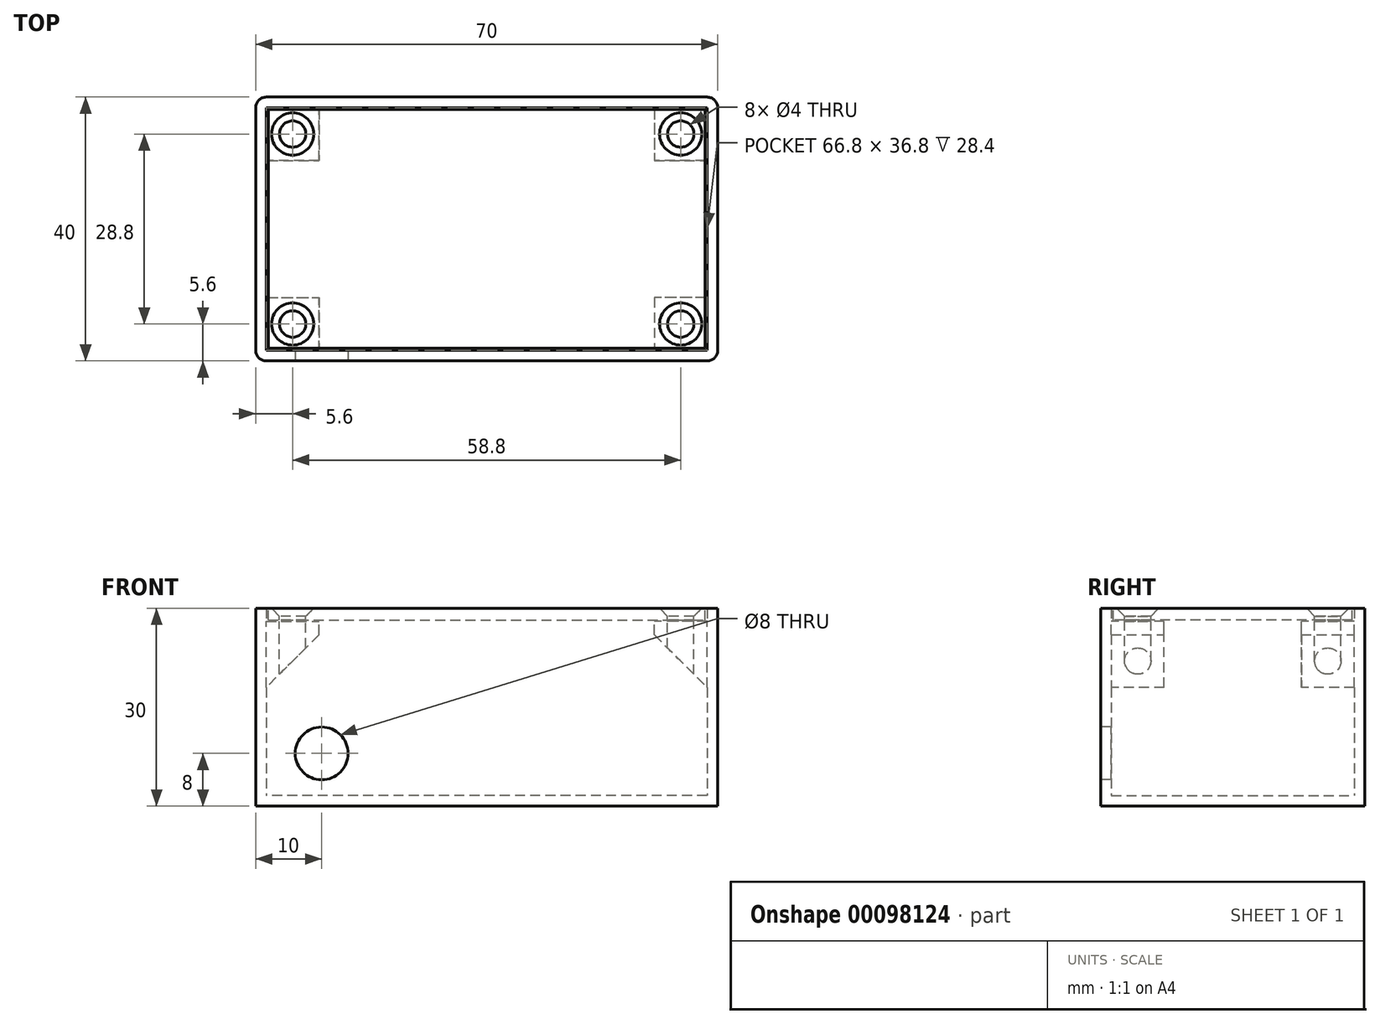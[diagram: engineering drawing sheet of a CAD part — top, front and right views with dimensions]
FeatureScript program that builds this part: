
annotation { "Feature Type Name" : "Feature", "Feature Type Description" : "" }
export const myFeature = defineFeature(function(context is Context, id is Id, definition is map)
    precondition{}
    {
        {
            var Q0;
            Q0=qCreatedBy(makeId("Top.planeOp"),FACE);
            var sketch = newSketch(context, id + "F0", { "sketchPlane" : qUnion([Q0])});
            skLineSegment(sketch, "E0.bottom", {"start": v(0, 0) * mm, "end": v(-70, 0) * mm});
            skLineSegment(sketch, "E0.top", {"start": v(0, 40) * mm, "end": v(-70, 40) * mm});
            skLineSegment(sketch, "E0.left", {"start": v(0, 0) * mm, "end": v(0, 40) * mm});
            skLineSegment(sketch, "E0.right", {"start": v(-70, 0) * mm, "end": v(-70, 40) * mm});
            skSolve(sketch);
        }
        {
            var Q0;
            Q0=makeQuery(id+"F0.imprint","IMPRINT",FACE,{"disambiguationData":[TD([[makeQuery(id+"F0.imprint","IMPRINT",EDGE,{"derivedFrom":sQuery(id+"F0.wireOp",EDGE,"E0.bottom")}),-1.0]])]});
            extrude(context, id + "F1", {"entities" : qUnion([Q0]), "depth" : 30 * mm});
        }
        {
            var Q0;
            Q0=makeQuery(id+"F1.opExtrude","CAP_FACE",FACE,{"disambiguationData":[OSD([sQuery(id+"F0.wireOp",EDGE,"E0.bottom"),sQuery(id+"F0.wireOp",EDGE,"E0.top"),sQuery(id+"F0.wireOp",EDGE,"E0.left"),sQuery(id+"F0.wireOp",EDGE,"E0.right")])],"isStart":false});
            shell(context, id + "F2", {"entities" : qUnion([Q0]), "thickness" : 1.6 * mm});
        }
        {
            var Q0;
            Q0=makeQuery(id+"F1.opExtrude","CAP_FACE",FACE,{"disambiguationData":[OSD([sQuery(id+"F0.wireOp",EDGE,"E0.bottom"),sQuery(id+"F0.wireOp",EDGE,"E0.top"),sQuery(id+"F0.wireOp",EDGE,"E0.left"),sQuery(id+"F0.wireOp",EDGE,"E0.right")])],"isStart":false});
            cPlane(context, id + "F3", {"entities" : qUnion([Q0]), "cplaneType" : CPlaneType.OFFSET, "offset" : 2 * mm, "oppositeDirection" : true, "width" : 150 * mm, "height" : 150 * mm});
        }
        {
            var Q0;
            Q0=qCreatedBy(id+"F3.planeOp",FACE);
            var sketch = newSketch(context, id + "F4", { "sketchPlane" : qUnion([Q0])});
            skLineSegment(sketch, "E1.bottom", {"start": v(-68.4, 38.4) * mm, "end": v(-60.4, 38.4) * mm});
            skLineSegment(sketch, "E1.top", {"start": v(-68.4, 30.4) * mm, "end": v(-60.4, 30.4) * mm});
            skLineSegment(sketch, "E1.left", {"start": v(-68.4, 38.4) * mm, "end": v(-68.4, 30.4) * mm});
            skLineSegment(sketch, "E1.right", {"start": v(-60.4, 38.4) * mm, "end": v(-60.4, 30.4) * mm});
            skLineSegment(sketch, "E2.bottom", {"start": v(-1.6, 38.4) * mm, "end": v(-9.6, 38.4) * mm});
            skLineSegment(sketch, "E2.top", {"start": v(-1.6, 30.4) * mm, "end": v(-9.6, 30.4) * mm});
            skLineSegment(sketch, "E2.left", {"start": v(-1.6, 38.4) * mm, "end": v(-1.6, 30.4) * mm});
            skLineSegment(sketch, "E2.right", {"start": v(-9.6, 38.4) * mm, "end": v(-9.6, 30.4) * mm});
            skLineSegment(sketch, "E3.bottom", {"start": v(-68.4, 9.6) * mm, "end": v(-60.4, 9.6) * mm});
            skLineSegment(sketch, "E3.top", {"start": v(-68.4, 1.6) * mm, "end": v(-60.4, 1.6) * mm});
            skLineSegment(sketch, "E3.left", {"start": v(-68.4, 9.6) * mm, "end": v(-68.4, 1.6) * mm});
            skLineSegment(sketch, "E3.right", {"start": v(-60.4, 9.6) * mm, "end": v(-60.4, 1.6) * mm});
            skLineSegment(sketch, "E4.bottom", {"start": v(-1.6, 9.6) * mm, "end": v(-9.6, 9.6) * mm});
            skLineSegment(sketch, "E4.top", {"start": v(-1.6, 1.6) * mm, "end": v(-9.6, 1.6) * mm});
            skLineSegment(sketch, "E4.left", {"start": v(-1.6, 9.6) * mm, "end": v(-1.6, 1.6) * mm});
            skLineSegment(sketch, "E4.right", {"start": v(-9.6, 9.6) * mm, "end": v(-9.6, 1.6) * mm});
            skCircle(sketch, "E5", {"center": v(-64.4, 34.4) * mm, "radius": 2 * mm});
            skPoint(sketch, "E5.centerSnap0", {"position": v(-64.4, 38.4) * mm});
            skPoint(sketch, "E5.centerSnap1", {"position": v(-60.4, 34.4) * mm});
            skCircle(sketch, "E6", {"center": v(-5.6, 34.4) * mm, "radius": 2 * mm});
            skPoint(sketch, "E6.centerSnap0", {"position": v(-5.6, 38.4) * mm});
            skPoint(sketch, "E6.centerSnap1", {"position": v(-1.6, 34.4) * mm});
            skCircle(sketch, "E7", {"center": v(-5.6, 5.6) * mm, "radius": 2 * mm});
            skPoint(sketch, "E7.centerSnap0", {"position": v(-5.6, 9.6) * mm});
            skPoint(sketch, "E7.centerSnap1", {"position": v(-1.6, 5.6) * mm});
            skCircle(sketch, "E8", {"center": v(-64.4, 5.6) * mm, "radius": 2 * mm});
            skPoint(sketch, "E8.centerSnap0", {"position": v(-60.4, 5.6) * mm});
            skPoint(sketch, "E8.centerSnap1", {"position": v(-64.4, 9.6) * mm});
            skSolve(sketch);
        }
        {
            var Q0;
            Q0 = qSketchRegion(id + "F4", true);
            extrude(context, id + "F5", {"entities" : qUnion([Q0]), "operationType" : NewBodyOperationType.ADD, "oppositeDirection" : true, "depth" : 10 * mm});
        }
        {
            var Q0;
            Q0=makeQuery(id+"F5.opExtrude","CAP_EDGE",EDGE,{"disambiguationData":[OSD([sQuery(id+"F4.wireOp",EDGE,"E1.right")])],"isStart":false});
            var Q1;
            Q1=makeQuery(id+"F5.opExtrude","CAP_EDGE",EDGE,{"disambiguationData":[OSD([sQuery(id+"F4.wireOp",EDGE,"E3.right")])],"isStart":false});
            var Q2;
            Q2=makeQuery(id+"F5.opExtrude","CAP_EDGE",EDGE,{"disambiguationData":[OSD([sQuery(id+"F4.wireOp",EDGE,"E2.right")])],"isStart":false});
            var Q3;
            Q3=makeQuery(id+"F5.opExtrude","CAP_EDGE",EDGE,{"disambiguationData":[OSD([sQuery(id+"F4.wireOp",EDGE,"E4.right")])],"isStart":false});
            chamfer(context, id + "F6", {"entities" : qUnion([Q0, Q1, Q2, Q3]), "width" : 8 * mm, "tangentPropagation" : true});
        }
        {
            var Q0;
            Q0=makeQuery(id+"F1.opExtrude","SWEPT_FACE",FACE,{"disambiguationData":[OSD([sQuery(id+"F0.wireOp",EDGE,"E0.bottom")])]});
            var sketch = newSketch(context, id + "F7", { "sketchPlane" : qUnion([Q0])});
            skCircle(sketch, "E9", {"center": v(-60, 8) * mm, "radius": 4 * mm});
            skSolve(sketch);
        }
        {
            var Q0;
            Q0 = qSketchRegion(id + "F7", true);
            extrude(context, id + "F8", {"entities" : qUnion([Q0]), "operationType" : NewBodyOperationType.REMOVE, "oppositeDirection" : true, "depth" : 25 * mm});
        }
        {
            var Q0;
            Q0=makeQuery(id+"F1.opExtrude","CAP_FACE",FACE,{"disambiguationData":[OSD([sQuery(id+"F0.wireOp",EDGE,"E0.bottom"),sQuery(id+"F0.wireOp",EDGE,"E0.top"),sQuery(id+"F0.wireOp",EDGE,"E0.left"),sQuery(id+"F0.wireOp",EDGE,"E0.right")])],"isStart":false});
            var sketch = newSketch(context, id + "F9", { "sketchPlane" : qUnion([Q0])});
            skLineSegment(sketch, "E10.bottom", {"start": v(-68.1, 38.1) * mm, "end": v(-1.9, 38.1) * mm});
            skLineSegment(sketch, "E10.top", {"start": v(-68.1, 1.9) * mm, "end": v(-1.9, 1.9) * mm});
            skLineSegment(sketch, "E10.left", {"start": v(-68.1, 38.1) * mm, "end": v(-68.1, 1.9) * mm});
            skLineSegment(sketch, "E10.right", {"start": v(-1.9, 38.1) * mm, "end": v(-1.9, 1.9) * mm});
            skCircle(sketch, "E11", {"center": v(-64.4, 34.4) * mm, "radius": 2 * mm});
            skCircle(sketch, "E12", {"center": v(-5.6, 34.4) * mm, "radius": 2 * mm});
            skCircle(sketch, "E13", {"center": v(-5.6, 5.6) * mm, "radius": 2 * mm});
            skCircle(sketch, "E14", {"center": v(-64.4, 5.6) * mm, "radius": 2 * mm});
            skSolve(sketch);
        }
        {
            var Q0;
            Q0 = qSketchRegion(id + "F9", true);
            extrude(context, id + "F10", {"entities" : qUnion([Q0]), "oppositeDirection" : true, "depth" : 1.8 * mm});
        }
        {
            var Q0;
            Q0=makeQuery(id+"F10.opExtrude","CAP_EDGE",EDGE,{"disambiguationData":[OSD([sQuery(id+"F9.wireOp",EDGE,"E13")])],"isStart":true});
            var Q1;
            Q1=makeQuery(id+"F10.opExtrude","CAP_EDGE",EDGE,{"disambiguationData":[OSD([sQuery(id+"F9.wireOp",EDGE,"E14")])],"isStart":true});
            var Q2;
            Q2=makeQuery(id+"F10.opExtrude","CAP_EDGE",EDGE,{"disambiguationData":[OSD([sQuery(id+"F9.wireOp",EDGE,"E11")])],"isStart":true});
            var Q3;
            Q3=makeQuery(id+"F10.opExtrude","CAP_EDGE",EDGE,{"disambiguationData":[OSD([sQuery(id+"F9.wireOp",EDGE,"E12")])],"isStart":true});
            chamfer(context, id + "F11", {"entities" : qUnion([Q0, Q1, Q2, Q3]), "width" : 1.2 * mm, "tangentPropagation" : true});
        }
        {
            var Q0;
            Q0=makeQuery(id+"F1.opExtrude","SWEPT_EDGE",EDGE,{"disambiguationData":[OSD([sQuery(id+"F0.wireOp",EDGE,"E0.bottom"),sQuery(id+"F0.wireOp",EDGE,"E0.right")])]});
            var Q1;
            Q1=makeQuery(id+"F1.opExtrude","SWEPT_EDGE",EDGE,{"disambiguationData":[OSD([sQuery(id+"F0.wireOp",EDGE,"E0.top"),sQuery(id+"F0.wireOp",EDGE,"E0.right")])]});
            var Q2;
            Q2=makeQuery(id+"F1.opExtrude","SWEPT_EDGE",EDGE,{"disambiguationData":[OSD([sQuery(id+"F0.wireOp",EDGE,"E0.bottom"),sQuery(id+"F0.wireOp",EDGE,"E0.left")])]});
            var Q3;
            Q3=makeQuery(id+"F1.opExtrude","SWEPT_EDGE",EDGE,{"disambiguationData":[OSD([sQuery(id+"F0.wireOp",EDGE,"E0.top"),sQuery(id+"F0.wireOp",EDGE,"E0.left")])]});
            fillet(context, id + "F12", {"entities" : qUnion([Q0, Q1, Q2, Q3]), "radius" : 1.6 * mm, "tangentPropagation" : true, "allowEdgeOverflow" : false});
        }
    });
